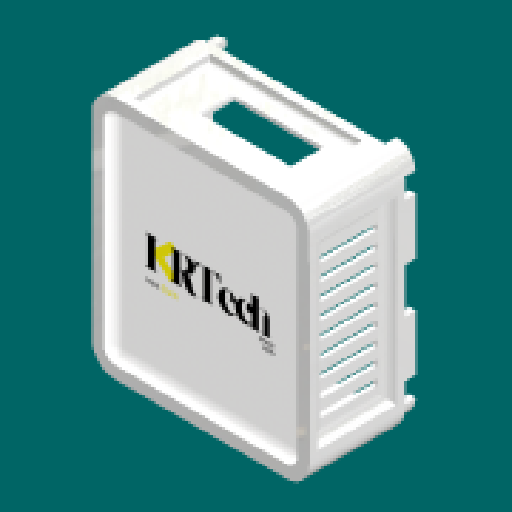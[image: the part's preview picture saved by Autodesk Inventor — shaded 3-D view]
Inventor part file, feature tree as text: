
AUTODESK INVENTOR PART (.ipt)
format: ipt  version: 2025.2 (Build 292293000, 293)  size: 672,256 bytes
history: native  units: mm
features: reference x42, sketch x14, extrude x12, other x6, fillet x3, plane x2, projected_geometry x1
ambient origin geometry x8: Origin, YZ Plane, XZ Plane, XY Plane, X Axis, Y Axis, Z Axis, Center Point
bodies: Solid1 (feature_tree)
feature tree (80):
  plane  "Work Plane1"
  extrude  "Extrusion1"  Depth=6.0mm TaperAngle=0.0deg
  extrude  "Extrusion2"  Depth=4.0mm
  extrude  "Extrusion3"  Depth=3.0mm TaperAngle=0.0deg
  fillet  "Fillet1"  Radius=4.0mm
  extrude  "Extrusion4"  Depth=3.0mm TaperAngle=0.0deg
  extrude  "Extrusion5"  Depth=2.0mm
  fillet  "Fillet2"  [1 undecoded]
  extrude  "Extrusion6"  TaperAngle=0.0deg  [1 undecoded]
  extrude  "Extrusion7"  Depth=0.2mm
  extrude  "Extrusion8"  Depth=10.0mm TaperAngle=0.0deg
  extrude  "Extrusion9"  Depth=2.0mm
  extrude  "Extrusion10"  [1 undecoded]
  extrude  "Extrusion12"  [1 undecoded]
  extrude  "Extrusion13"  [1 undecoded]
  fillet  "Fillet4"  [1 undecoded]
  plane  "Work Plane2"
  other  "Decal1"
  sketch  "Sketch1"  dims[d0=30.93mm d1=0.0mm d2=6.0mm d3=0.0mm]
  reference  "Reference1"
  sketch  "Sketch2"  dims[d7=3.0mm d8=0.0mm d9=3.0mm d10=0.0mm d11=4.0mm]
  sketch  "Sketch3"  dims[d12=3.0mm d13=0.0mm d14=3.0mm d15=0.0mm]
  sketch  "Sketch4"  dims[d17=5.6mm d18=0.0mm d19=2.0mm]
  sketch  "Sketch5"  dims[d20=10.0mm d22=10.0mm d23=280.0mm d25=2.0mm d27=0.0mm d28=0.0mm]
  sketch  "Sketch6"  dims[d29=0.25mm d30=0.0mm d31=0.0mm]
  sketch  "Sketch7"  dims[d32=0.25mm d35=0.2mm]
  sketch  "Sketch8"  dims[d36=0.2mm d37=10.0mm d38=0.0mm]
  reference  "Reference2"
  reference  "Reference3"
  reference  "Reference4"
  reference  "Reference5"
  reference  "Reference6"
  reference  "Reference7"
  reference  "Reference8"
  reference  "Reference9"
  reference  "Reference10"
  reference  "Reference11"
  reference  "Reference12"
  reference  "Reference13"
  reference  "Reference14"
  reference  "Reference15"
  reference  "Reference16"
  reference  "Reference17"
  reference  "Reference18"
  reference  "Reference19"
  reference  "Reference20"
  reference  "Reference21"
  reference  "Reference22"
  reference  "Reference23"
  reference  "Reference24"
  reference  "Reference25"
  reference  "Reference26"
  reference  "Reference27"
  reference  "Reference28"
  reference  "Reference29"
  reference  "Reference30"
  reference  "Reference31"
  reference  "Reference32"
  reference  "Reference33"
  reference  "Reference34"
  reference  "Reference35"
  sketch  "Sketch9"  dims[d39=10.0mm d40=0.0mm d41=2.0mm]
  projected_geometry  "Projected Loop1"
  sketch  "Sketch Rectangular Pattern1"  dims[d4=3.0mm d5=0.0mm d6=4.0mm]
  sketch  "Sketch10"  dims[d42=5.75mm]
  reference  "Reference36"
  reference  "Reference37"
  reference  "Reference38"
  sketch  "Sketch12"
  reference  "Reference45"
  reference  "Reference46"
  sketch  "Sketch13"
  reference  "Reference47"
  reference  "Reference48"
  sketch  "Sketch14"
  other  "Image1"
  other  "<userpath>\Downloads\cassing_hardware\Assembly1.iam"
  other  "Assembly1.iam"
  other  "part1:1"
  other  "AVR_MasImam:1"
note: 6 required parameter values undecoded (feature->parameter linkage not recoverable at this tier; creation-order binding heuristic only, values carry confidence <= 0.55)
